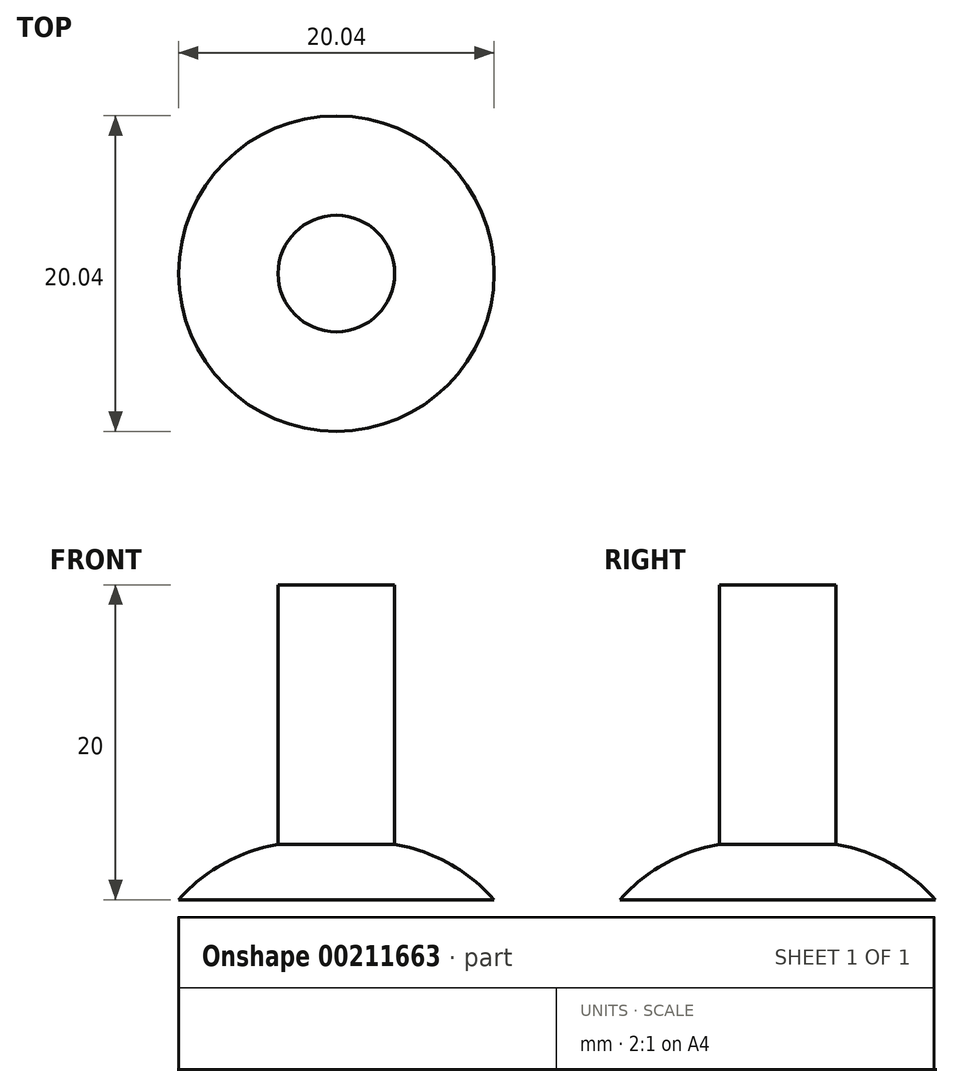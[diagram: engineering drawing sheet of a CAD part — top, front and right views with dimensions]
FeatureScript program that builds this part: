
annotation { "Feature Type Name" : "Feature", "Feature Type Description" : "" }
export const myFeature = defineFeature(function(context is Context, id is Id, definition is map)
    precondition{}
    {
        {
            var Q0;
            Q0=qCreatedBy(makeId("Front.planeOp"),FACE);
            var sketch = newSketch(context, id + "F0", { "sketchPlane" : qUnion([Q0])});
            skLineSegment(sketch, "E0", {"start": v(0, 0) * mm, "end": v(0, 3.5) * mm});
            skLineSegment(sketch, "E1", {"start": v(0, 0) * mm, "end": v(0, 9.33) * mm, "construction": true});
            skArc(sketch, "E2", {"start": v(10.02, 0) * mm, "mid": v(5.47, 3.06) * mm, "end": v(0, 3.5) * mm});
            skLineSegment(sketch, "E3", {"start": v(0, 0) * mm, "end": v(10.02, 0) * mm});
            skSolve(sketch);
        }
        {
            var Q0;
            Q0=makeQuery(id+"F0.imprint","IMPRINT",FACE,{"disambiguationData":[TD([[makeQuery(id+"F0.imprint","IMPRINT",EDGE,{"derivedFrom":sQuery(id+"F0.wireOp",EDGE,"E0")}),-1.0]])]});
            var Q1;
            Q1=sQuery(id+"F0.wireOp",EDGE,"E1");
            revolve(context, id + "F1", {"entities" : qUnion([Q0]), "axis" : qUnion([Q1]), "revolveType" : RevolveType.FULL});
        }
        {
            var Q0;
            Q0=qCreatedBy(makeId("Top.planeOp"),FACE);
            var sketch = newSketch(context, id + "F2", { "sketchPlane" : qUnion([Q0])});
            skCircle(sketch, "E4", {"center": v(0, 0) * mm, "radius": 3.7 * mm});
            skSolve(sketch);
        }
        {
            var Q0;
            Q0=qSketchRegion(id+"F2",true);
            extrude(context, id + "F3", {"entities" : qUnion([Q0]), "operationType" : NewBodyOperationType.ADD, "depth" : 20 * mm});
        }
    });
